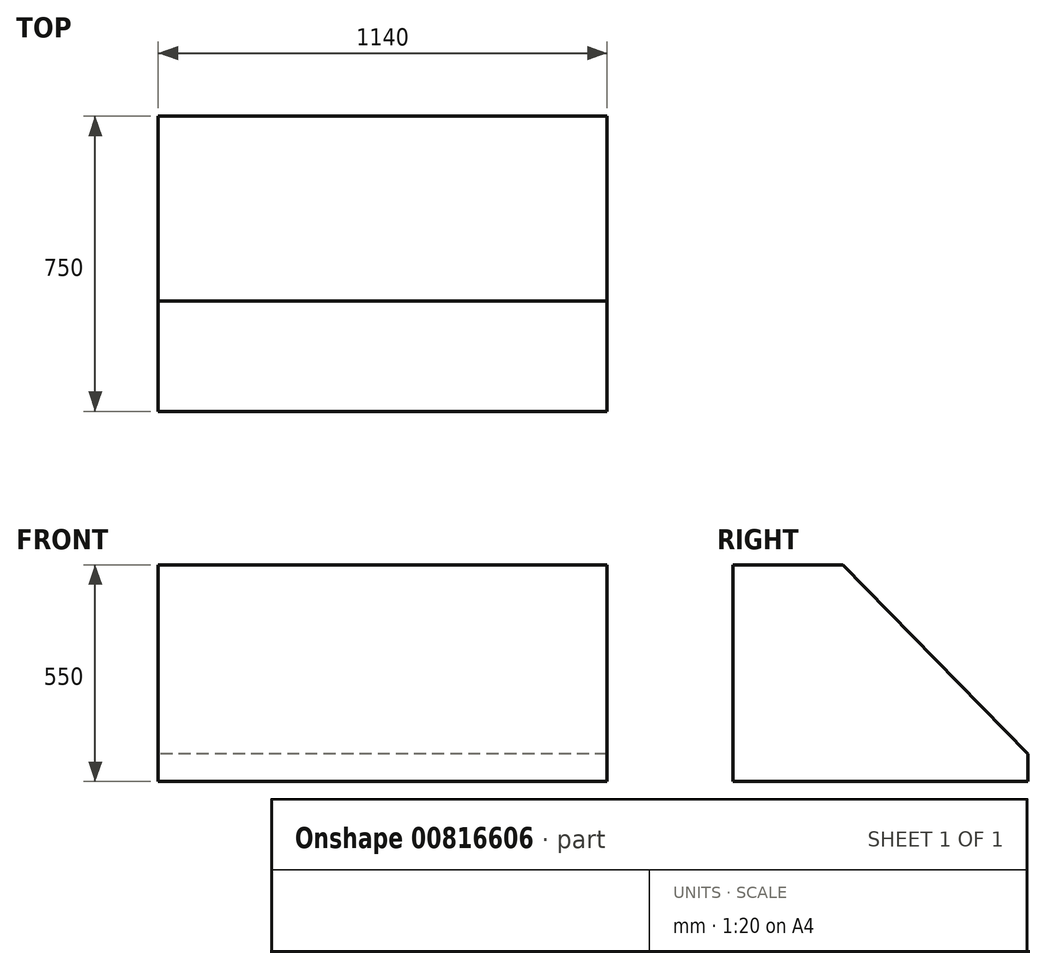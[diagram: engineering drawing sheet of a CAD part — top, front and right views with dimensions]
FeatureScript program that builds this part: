
annotation { "Feature Type Name" : "Feature", "Feature Type Description" : "" }
export const myFeature = defineFeature(function(context is Context, id is Id, definition is map)
    precondition{}
    {
        {
            var Q0;
            Q0=qCreatedBy(makeId("Right.planeOp"),FACE);
            var sketch = newSketch(context, id + "F0", { "sketchPlane" : qUnion([Q0])});
            skLineSegment(sketch, "E0", {"start": v(0, 0) * mm, "end": v(750, 0) * mm});
            skLineSegment(sketch, "E1", {"start": v(750, 0) * mm, "end": v(750, 70) * mm});
            skLineSegment(sketch, "E2", {"start": v(750, 70) * mm, "end": v(280, 550) * mm});
            skLineSegment(sketch, "E3", {"start": v(280, 550) * mm, "end": v(0, 550) * mm});
            skLineSegment(sketch, "E4", {"start": v(0, 550) * mm, "end": v(0, 0) * mm});
            skSolve(sketch);
        }
        {
            var Q0;
            Q0=makeQuery(id+"F0.imprint","IMPRINT",FACE,{"disambiguationData":[TD([[makeQuery(id+"F0.imprint","IMPRINT",EDGE,{"derivedFrom":sQuery(id+"F0.wireOp",EDGE,"E0")}),1.0]])]});
            extrude(context, id + "F1", {"entities" : qUnion([Q0]), "depth" : 1140 * mm, "offsetDistance" : 25 * mm});
        }
    });
